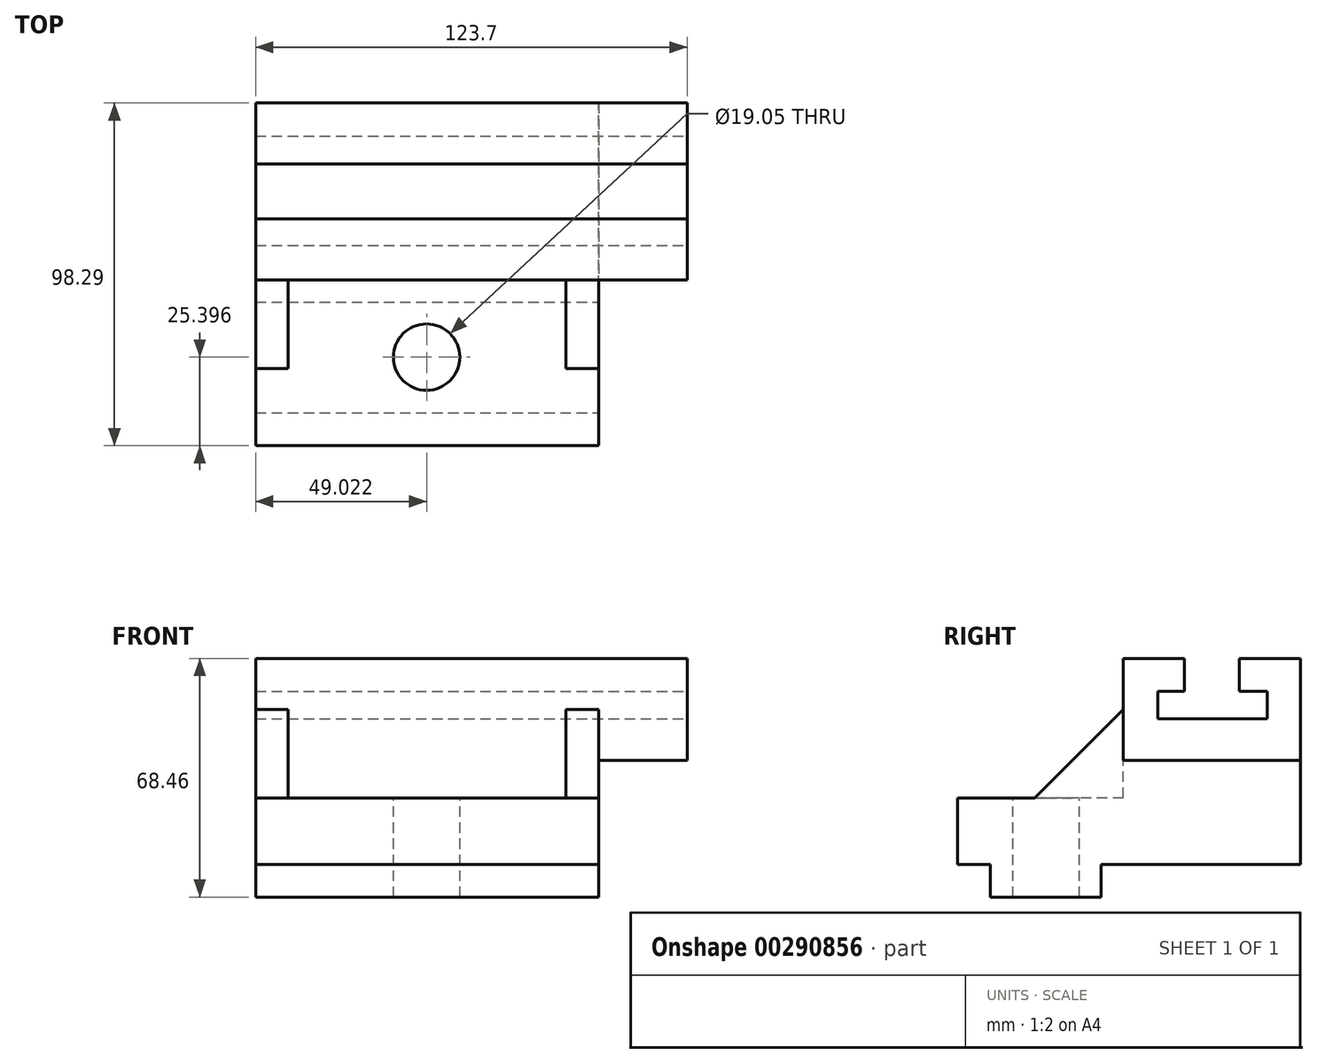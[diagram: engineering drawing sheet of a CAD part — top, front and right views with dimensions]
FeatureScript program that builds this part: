
annotation { "Feature Type Name" : "Feature", "Feature Type Description" : "" }
export const myFeature = defineFeature(function(context is Context, id is Id, definition is map)
    precondition{}
    {
        {
            var Q0;
            Q0=qCreatedBy(makeId("Right.planeOp"),FACE);
            var sketch = newSketch(context, id + "F0", { "sketchPlane" : qUnion([Q0])});
            skLineSegment(sketch, "E0", {"start": v(-9.9, 26.27) * mm, "end": v(40.9, 26.27) * mm});
            skLineSegment(sketch, "E1", {"start": v(40.9, 26.27) * mm, "end": v(40.9, 55.48) * mm});
            skLineSegment(sketch, "E2", {"start": v(-9.9, 26.27) * mm, "end": v(-9.9, 55.48) * mm});
            skLineSegment(sketch, "E3", {"start": v(40.9, 55.48) * mm, "end": v(-9.9, 55.48) * mm});
            skSolve(sketch);
        }
        {
            var Q0;
            Q0 = qSketchRegion(id + "F0", true);
            extrude(context, id + "F1", {"entities" : qUnion([Q0]), "depth" : 123.7 * mm});
        }
        {
            var Q0;
            Q0=makeQuery(id+"F1.opExtrude","CAP_FACE",FACE,{"disambiguationData":[OSD([sQuery(id+"F0.wireOp",EDGE,"E0"),sQuery(id+"F0.wireOp",EDGE,"E1"),sQuery(id+"F0.wireOp",EDGE,"E2"),sQuery(id+"F0.wireOp",EDGE,"E3")])],"isStart":false});
            var sketch = newSketch(context, id + "F2", { "sketchPlane" : qUnion([Q0])});
            skLineSegment(sketch, "E4", {"start": v(40.9, 26.27) * mm, "end": v(40.9, 38.2) * mm});
            skLineSegment(sketch, "E5", {"start": v(40.9, 55.48) * mm, "end": v(23.37, 55.48) * mm});
            skLineSegment(sketch, "E6", {"start": v(23.37, 55.48) * mm, "end": v(23.37, 46.08) * mm});
            skLineSegment(sketch, "E7", {"start": v(-9.9, 55.48) * mm, "end": v(7.62, 55.48) * mm});
            skLineSegment(sketch, "E8", {"start": v(7.62, 55.48) * mm, "end": v(7.62, 46.08) * mm});
            skLineSegment(sketch, "E9", {"start": v(-9.9, 26.27) * mm, "end": v(-0.38, 26.27) * mm});
            skLineSegment(sketch, "E10", {"start": v(40.9, 26.27) * mm, "end": v(31.37, 26.27) * mm});
            skLineSegment(sketch, "E11", {"start": v(7.62, 46.08) * mm, "end": v(0, 46.08) * mm});
            skLineSegment(sketch, "E12", {"start": v(0, 46.08) * mm, "end": v(0, 38.2) * mm});
            skLineSegment(sketch, "E13", {"start": v(0, 38.2) * mm, "end": v(31.37, 38.2) * mm});
            skLineSegment(sketch, "E14", {"start": v(31.37, 38.2) * mm, "end": v(31.37, 46.08) * mm});
            skLineSegment(sketch, "E15", {"start": v(31.37, 46.08) * mm, "end": v(23.37, 46.08) * mm});
            skSolve(sketch);
        }
        {
            var Q0;
            {var subQ1=sQuery(id+"F2.wireOp",EDGE,"E6");Q0=makeQuery(id+"F2.imprint","IMPRINT",FACE,{"disambiguationData":[TD([[makeQuery(id+"F2.imprint","IMPRINT",EDGE,{"derivedFrom":subQ1}),-1.0]])]});}
            extrude(context, id + "F3", {"entities" : qUnion([Q0]), "operationType" : NewBodyOperationType.REMOVE, "oppositeDirection" : true, "depth" : 123.7 * mm});
        }
        {
            var Q0;
            Q0=makeQuery(id+"F1.opExtrude","SWEPT_FACE",FACE,{"disambiguationData":[OSD([sQuery(id+"F0.wireOp",EDGE,"E2")])]});
            var sketch = newSketch(context, id + "F4", { "sketchPlane" : qUnion([Q0])});
            skLineSegment(sketch, "E16", {"start": v(0, 40.87) * mm, "end": v(0, 15.47) * mm});
            skLineSegment(sketch, "E17", {"start": v(0, 15.47) * mm, "end": v(98.3, 15.47) * mm});
            skLineSegment(sketch, "E18", {"start": v(98.3, 15.47) * mm, "end": v(98.3, 26.27) * mm});
            skSolve(sketch);
        }
        {
            var Q0;
            Q0 = qSketchRegion(id + "F4", true);
            var Q1;
            {var subQ3=sQuery(id+"F4.wireOp",EDGE,"E17");Q1=makeQuery(id+"F4.imprint","IMPRINT",FACE,{"disambiguationData":[TD([[makeQuery(id+"F4.imprint","IMPRINT",EDGE,{"derivedFrom":subQ3}),1.0]])]});}
            extrude(context, id + "F5", {"entities" : qUnion([Q0, Q1]), "operationType" : NewBodyOperationType.ADD, "oppositeDirection" : true, "depth" : 50.8 * mm});
        }
        {
            var Q0;
            Q0=makeQuery(id+"F5.boolean.opBoolean","MERGE",FACE,{"derivedFrom":[makeQuery(id+"F1.opExtrude","CAP_FACE",FACE,{"disambiguationData":[OSD([sQuery(id+"F0.wireOp",EDGE,"E0"),sQuery(id+"F0.wireOp",EDGE,"E1"),sQuery(id+"F0.wireOp",EDGE,"E2"),sQuery(id+"F0.wireOp",EDGE,"E3")])],"isStart":true}),makeQuery(id+"F5.opExtrude","SWEPT_FACE",FACE,{"disambiguationData":[OSD([sQuery(id+"F4.wireOp",EDGE,"E16")])]})]});
            var sketch = newSketch(context, id + "F6", { "sketchPlane" : qUnion([Q0])});
            skLineSegment(sketch, "E19", {"start": v(-40.9, 15.47) * mm, "end": v(57.4, 15.47) * mm});
            skPoint(sketch, "E19.endSnap0", {"position": v(-15.5, 15.47) * mm});
            skLineSegment(sketch, "E20", {"start": v(57.4, 15.47) * mm, "end": v(57.4, -12.98) * mm});
            skLineSegment(sketch, "E21", {"start": v(57.4, -12.98) * mm, "end": v(-40.9, -12.98) * mm});
            skLineSegment(sketch, "E22", {"start": v(-40.9, -12.98) * mm, "end": v(-40.9, 15.47) * mm});
            skSolve(sketch);
        }
        {
            var Q0;
            Q0 = qSketchRegion(id + "F6", true);
            extrude(context, id + "F7", {"entities" : qUnion([Q0]), "operationType" : NewBodyOperationType.ADD, "oppositeDirection" : true, "depth" : 98.3 * mm});
        }
        {
            var Q0;
            Q0=makeQuery(id+"F7.boolean.opBoolean","MERGE",FACE,{"derivedFrom":[makeQuery(id+"F5.boolean.opBoolean","MERGE",FACE,{"derivedFrom":[makeQuery(id+"F1.opExtrude","CAP_FACE",FACE,{"disambiguationData":[OSD([sQuery(id+"F0.wireOp",EDGE,"E0"),sQuery(id+"F0.wireOp",EDGE,"E1"),sQuery(id+"F0.wireOp",EDGE,"E2"),sQuery(id+"F0.wireOp",EDGE,"E3")])],"isStart":true}),makeQuery(id+"F5.opExtrude","SWEPT_FACE",FACE,{"disambiguationData":[OSD([sQuery(id+"F4.wireOp",EDGE,"E16")])]})]}),makeQuery(id+"F7.opExtrude","CAP_FACE",FACE,{"disambiguationData":[OSD([sQuery(id+"F6.wireOp",EDGE,"E19"),sQuery(id+"F6.wireOp",EDGE,"E20"),sQuery(id+"F6.wireOp",EDGE,"E21"),sQuery(id+"F6.wireOp",EDGE,"E22")])],"isStart":true})]});
            var sketch = newSketch(context, id + "F8", { "sketchPlane" : qUnion([Q0])});
            skLineSegment(sketch, "E23", {"start": v(9.9, 15.47) * mm, "end": v(9.9, 40.87) * mm});
            skLineSegment(sketch, "E24", {"start": v(9.9, 40.87) * mm, "end": v(35.3, 15.47) * mm});
            skSolve(sketch);
        }
        {
            var Q0;
            Q0=makeQuery(id+"F7.boolean.opBoolean","MERGE",FACE,{"derivedFrom":[makeQuery(id+"F5.opExtrude","SWEPT_FACE",FACE,{"disambiguationData":[OSD([sQuery(id+"F4.wireOp",EDGE,"E18")])]}),makeQuery(id+"F7.opExtrude","CAP_FACE",FACE,{"disambiguationData":[OSD([sQuery(id+"F6.wireOp",EDGE,"E19"),sQuery(id+"F6.wireOp",EDGE,"E20"),sQuery(id+"F6.wireOp",EDGE,"E21"),sQuery(id+"F6.wireOp",EDGE,"E22")])],"isStart":false})]});
            var sketch = newSketch(context, id + "F9", { "sketchPlane" : qUnion([Q0])});
            skLineSegment(sketch, "E25", {"start": v(-9.9, 15.47) * mm, "end": v(-9.9, 40.87) * mm});
            skLineSegment(sketch, "E26", {"start": v(-9.9, 15.47) * mm, "end": v(-35.3, 15.47) * mm});
            skLineSegment(sketch, "E27", {"start": v(-9.9, 40.87) * mm, "end": v(-35.3, 15.47) * mm});
            skSolve(sketch);
        }
        {
            var Q0;
            {var subQ2=sQuery(id+"F9.wireOp",EDGE,"E26");Q0=makeQuery(id+"F9.imprint","IMPRINT",FACE,{"disambiguationData":[TD([[makeQuery(id+"F9.imprint","IMPRINT",EDGE,{"derivedFrom":subQ2}),-1.0]])]});}
            extrude(context, id + "F10", {"entities" : qUnion([Q0]), "operationType" : NewBodyOperationType.ADD, "oppositeDirection" : true, "depth" : 9.4 * mm});
        }
        {
            var Q0;
            {var subQ0=sQuery(id+"F8.wireOp",EDGE,"E23");Q0=makeQuery(id+"F8.imprint","IMPRINT",FACE,{"disambiguationData":[TD([[makeQuery(id+"F8.imprint","IMPRINT",EDGE,{"derivedFrom":subQ0}),-1.0]])]});}
            extrude(context, id + "F11", {"entities" : qUnion([Q0]), "operationType" : NewBodyOperationType.ADD, "oppositeDirection" : true, "depth" : 9.4 * mm});
        }
        {
            var Q0;
            Q0=makeQuery(id+"F10.boolean.opBoolean","MERGE",FACE,{"derivedFrom":[makeQuery(id+"F7.boolean.opBoolean","MERGE",FACE,{"derivedFrom":[makeQuery(id+"F5.opExtrude","SWEPT_FACE",FACE,{"disambiguationData":[OSD([sQuery(id+"F4.wireOp",EDGE,"E18")])]}),makeQuery(id+"F7.opExtrude","CAP_FACE",FACE,{"disambiguationData":[OSD([sQuery(id+"F6.wireOp",EDGE,"E19"),sQuery(id+"F6.wireOp",EDGE,"E20"),sQuery(id+"F6.wireOp",EDGE,"E21"),sQuery(id+"F6.wireOp",EDGE,"E22")])],"isStart":false})]}),makeQuery(id+"F10.opExtrude","CAP_FACE",FACE,{"disambiguationData":[OSD([sQuery(id+"F9.wireOp",EDGE,"E25"),sQuery(id+"F9.wireOp",EDGE,"E26"),sQuery(id+"F9.wireOp",EDGE,"E27")])],"isStart":true})]});
            var sketch = newSketch(context, id + "F12", { "sketchPlane" : qUnion([Q0])});
            skLineSegment(sketch, "E28", {"start": v(-57.4, -12.98) * mm, "end": v(-48, -12.98) * mm});
            skLineSegment(sketch, "E29", {"start": v(-57.4, -12.98) * mm, "end": v(-57.4, -3.58) * mm});
            skLineSegment(sketch, "E30", {"start": v(-57.4, -3.58) * mm, "end": v(-48, -3.58) * mm});
            skLineSegment(sketch, "E31", {"start": v(-48, -3.58) * mm, "end": v(-48, -12.98) * mm});
            skSolve(sketch);
        }
        {
            var Q0;
            Q0 = qSketchRegion(id + "F12", true);
            extrude(context, id + "F13", {"entities" : qUnion([Q0]), "operationType" : NewBodyOperationType.REMOVE, "oppositeDirection" : true, "depth" : 98.3 * mm});
        }
        {
            var Q0;
            Q0=makeQuery(id+"F10.boolean.opBoolean","MERGE",FACE,{"derivedFrom":[makeQuery(id+"F7.boolean.opBoolean","MERGE",FACE,{"derivedFrom":[makeQuery(id+"F5.opExtrude","SWEPT_FACE",FACE,{"disambiguationData":[OSD([sQuery(id+"F4.wireOp",EDGE,"E18")])]}),makeQuery(id+"F7.opExtrude","CAP_FACE",FACE,{"disambiguationData":[OSD([sQuery(id+"F6.wireOp",EDGE,"E19"),sQuery(id+"F6.wireOp",EDGE,"E20"),sQuery(id+"F6.wireOp",EDGE,"E21"),sQuery(id+"F6.wireOp",EDGE,"E22")])],"isStart":false})]}),makeQuery(id+"F10.opExtrude","CAP_FACE",FACE,{"disambiguationData":[OSD([sQuery(id+"F9.wireOp",EDGE,"E25"),sQuery(id+"F9.wireOp",EDGE,"E26"),sQuery(id+"F9.wireOp",EDGE,"E27")])],"isStart":true})]});
            var sketch = newSketch(context, id + "F14", { "sketchPlane" : qUnion([Q0])});
            skLineSegment(sketch, "E32", {"start": v(-48, -12.98) * mm, "end": v(-16.26, -12.98) * mm});
            skLineSegment(sketch, "E33", {"start": v(-16.26, -12.98) * mm, "end": v(-16.26, -3.58) * mm});
            skLineSegment(sketch, "E34", {"start": v(-16.26, -3.58) * mm, "end": v(40.9, -3.58) * mm});
            skSolve(sketch);
        }
        {
            var Q0;
            {var subQ0=sQuery(id+"F14.wireOp",EDGE,"E33");Q0=makeQuery(id+"F14.imprint","IMPRINT",FACE,{"disambiguationData":[TD([[makeQuery(id+"F14.imprint","IMPRINT",EDGE,{"derivedFrom":subQ0}),-1.0]])]});}
            extrude(context, id + "F15", {"entities" : qUnion([Q0]), "operationType" : NewBodyOperationType.REMOVE, "oppositeDirection" : true, "depth" : 98.3 * mm});
        }
        {
            var Q0;
            Q0=makeQuery(id+"F7.opExtrude","SWEPT_FACE",FACE,{"disambiguationData":[OSD([sQuery(id+"F6.wireOp",EDGE,"E19")])]});
            var sketch = newSketch(context, id + "F16", { "sketchPlane" : qUnion([Q0])});
            skCircle(sketch, "E35", {"center": v(49.02, -32) * mm, "radius": 9.53 * mm});
            skSolve(sketch);
        }
        {
            var Q0;
            Q0 = qSketchRegion(id + "F16", true);
            extrude(context, id + "F17", {"entities" : qUnion([Q0]), "operationType" : NewBodyOperationType.REMOVE, "oppositeDirection" : true, "depth" : 28.45 * mm});
        }
    });
